# Revit family: Layout-Teknion-Zones_Collaborative_Twin-R2022
name_source: partatom
category: Furniture Systems
units: mm (PartAtom-declared; Revit-internal decimal feet)

## family parameters
Always vertical = Yes
Cut with Voids When Loaded = No
OmniClass Number = 23.40.70.14.64.21
OmniClass Title = Systems Furniture
Part Type = Normal
Room Calculation Point = No
Round Connector Dimension = Use Diameter
Shared = No
Work Plane-Based = No

## types (1)
- Collaborative Zone Twin
    Assembly Code = E2020200
    Default Elevation = 0"
    Depth = 75 1/2"
    Description = 100" wide x 75 1/2" deep, 100" Diameter
    Height = 55"
    Manufacturer = Teknion
    Manufacturer Fax = 416.661.4586
    Model = Collaborative Zone - Twin
    Number of Poles = 1
    Part Number = ZNCCT
    Product Documentation Link = https://www.teknion.com
    Product Line = Zones
    Product Page URL = http://teknionplanningtool.com
    Sustainability Data = http://www.teknion.com
    URL = http://www.teknion.com
    Warranty = http://www.teknion.com
    Width = 100"

## geometry (parser evidence)
native form markers: Blend x28, Sweep x31
no freeform markers — native parametric forms only
